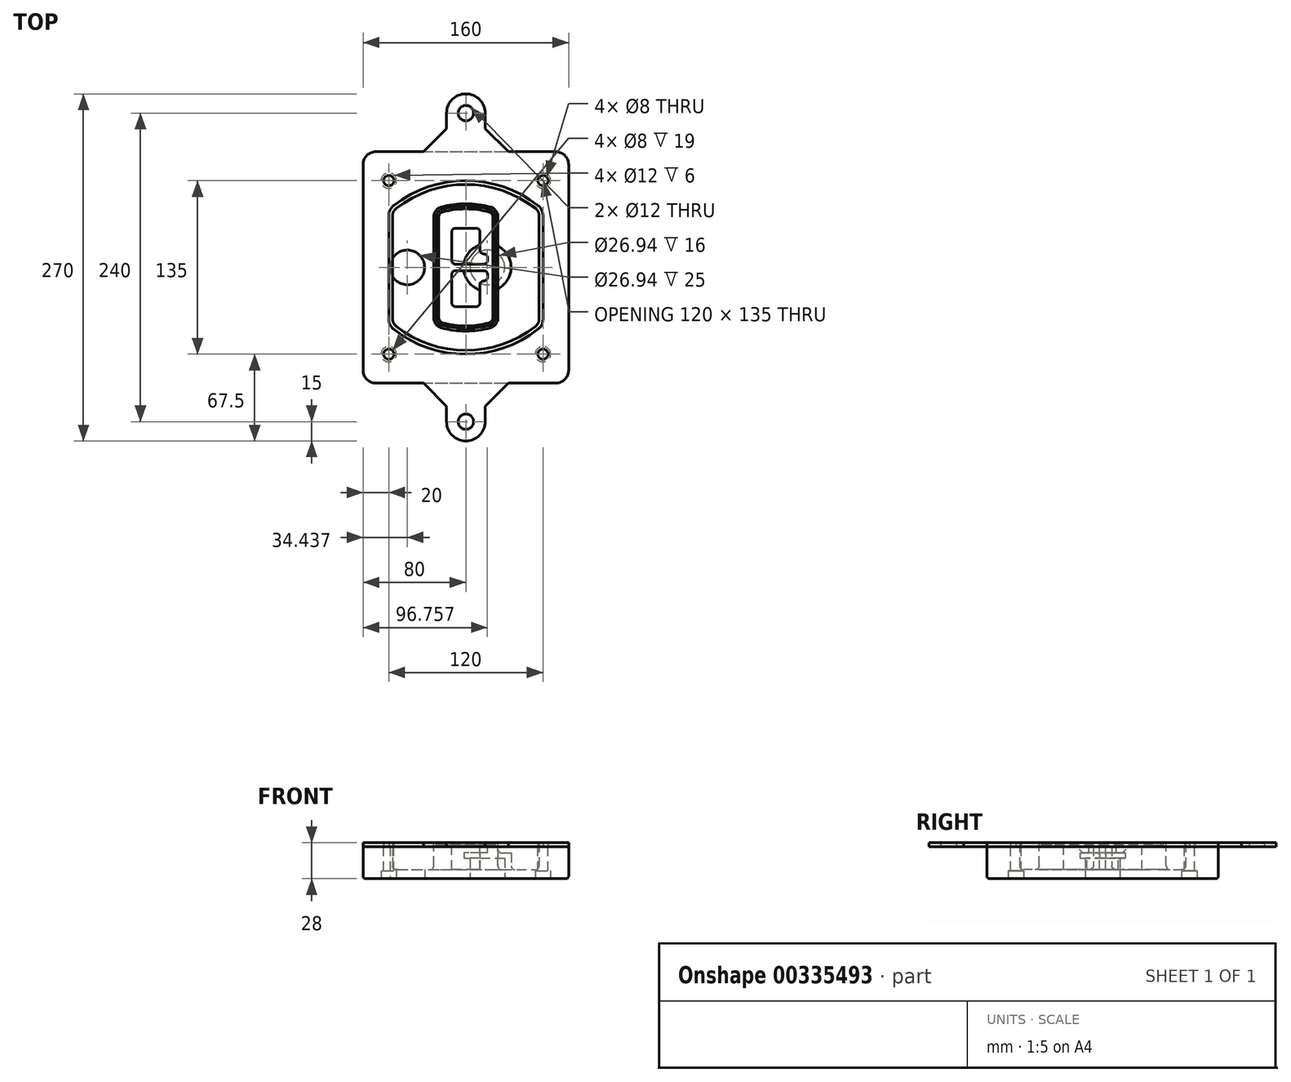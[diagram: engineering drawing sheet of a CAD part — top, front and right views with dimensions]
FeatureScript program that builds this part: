
annotation { "Feature Type Name" : "Feature", "Feature Type Description" : "" }
export const myFeature = defineFeature(function(context is Context, id is Id, definition is map)
    precondition{}
    {
        {
            var Q0;
            Q0=qCreatedBy(makeId("Top.planeOp"),FACE);
            var sketch = newSketch(context, id + "F0", { "sketchPlane" : qUnion([Q0])});
            skPoint(sketch, "E0.rect.middle", {"position": v(0, 0) * mm});
            skLineSegment(sketch, "E1.bottom", {"start": v(-70, -90) * mm, "end": v(70, -90) * mm});
            skLineSegment(sketch, "E1.top", {"start": v(-70, 90) * mm, "end": v(70, 90) * mm});
            skLineSegment(sketch, "E1.left", {"start": v(-80, -80) * mm, "end": v(-80, 80) * mm});
            skLineSegment(sketch, "E1.right", {"start": v(80, -80) * mm, "end": v(80, 80) * mm});
            skLineSegment(sketch, "E2", {"start": v(-80, 90) * mm, "end": v(80, -90) * mm, "construction": true});
            skLineSegment(sketch, "E3", {"start": v(80, 90) * mm, "end": v(-80, -90) * mm, "construction": true});
            skCircle(sketch, "E4", {"center": v(-60, 67.5) * mm, "radius": 4 * mm});
            skCircle(sketch, "E5", {"center": v(60, 67.5) * mm, "radius": 4 * mm});
            skCircle(sketch, "E6", {"center": v(60, -67.5) * mm, "radius": 4 * mm});
            skCircle(sketch, "E7", {"center": v(-60, -67.5) * mm, "radius": 4 * mm});
            skLineSegment(sketch, "E8", {"start": v(-60, 67.5) * mm, "end": v(60, 67.5) * mm, "construction": true});
            skLineSegment(sketch, "E9", {"start": v(60, 67.5) * mm, "end": v(60, -67.5) * mm, "construction": true});
            skLineSegment(sketch, "E10", {"start": v(60, -67.5) * mm, "end": v(-60, -67.5) * mm, "construction": true});
            skLineSegment(sketch, "E11", {"start": v(-60, -67.5) * mm, "end": v(-60, 67.5) * mm, "construction": true});
            skLineSegment(sketch, "E12", {"start": v(-60, 40.3) * mm, "end": v(-60, -40.3) * mm});
            skLineSegment(sketch, "E13", {"start": v(60, 40.3) * mm, "end": v(60, -40.3) * mm});
            skArc(sketch, "E14", {"start": v(56.15, 48.18) * mm, "mid": v(0, 67.5) * mm, "end": v(-56.15, 48.18) * mm});
            skArc(sketch, "E15", {"start": v(-56.15, -48.18) * mm, "mid": v(0, -67.5) * mm, "end": v(56.15, -48.18) * mm});
            skLineSegment(sketch, "E16", {"start": v(-60, 0) * mm, "end": v(60, 0) * mm, "construction": true});
            skPoint(sketch, "E17.visualSharp", {"position": v(-60, -45) * mm});
            skArc(sketch, "E17.filletArc", {"start": v(-60, -40.3) * mm, "mid": v(-58.99, -44.68) * mm, "end": v(-56.15, -48.18) * mm});
            skPoint(sketch, "E18.visualSharp", {"position": v(-60, 45) * mm});
            skArc(sketch, "E18.filletArc", {"start": v(-56.15, 48.18) * mm, "mid": v(-58.99, 44.68) * mm, "end": v(-60, 40.3) * mm});
            skPoint(sketch, "E19.visualSharp", {"position": v(60, 45) * mm});
            skArc(sketch, "E19.filletArc", {"start": v(60, 40.3) * mm, "mid": v(58.99, 44.68) * mm, "end": v(56.15, 48.18) * mm});
            skPoint(sketch, "E20.visualSharp", {"position": v(60, -45) * mm});
            skArc(sketch, "E20.filletArc", {"start": v(56.15, -48.18) * mm, "mid": v(58.99, -44.68) * mm, "end": v(60, -40.3) * mm});
            skPoint(sketch, "E21.visualSharp", {"position": v(-80, 90) * mm});
            skArc(sketch, "E21.filletArc", {"start": v(-70, 90) * mm, "mid": v(-77.07, 87.07) * mm, "end": v(-80, 80) * mm});
            skPoint(sketch, "E22.visualSharp", {"position": v(80, 90) * mm});
            skArc(sketch, "E22.filletArc", {"start": v(80, 80) * mm, "mid": v(77.07, 87.07) * mm, "end": v(70, 90) * mm});
            skPoint(sketch, "E23.visualSharp", {"position": v(80, -90) * mm});
            skArc(sketch, "E23.filletArc", {"start": v(70, -90) * mm, "mid": v(77.07, -87.07) * mm, "end": v(80, -80) * mm});
            skPoint(sketch, "E24.visualSharp", {"position": v(-80, -90) * mm});
            skArc(sketch, "E24.filletArc", {"start": v(-80, -80) * mm, "mid": v(-77.07, -87.07) * mm, "end": v(-70, -90) * mm});
            skArc(sketch, "E25.0", {"start": v(57, 40.3) * mm, "mid": v(56.3, 43.36) * mm, "end": v(54.3, 45.81) * mm});
            skLineSegment(sketch, "E25.1", {"start": v(57, 40.3) * mm, "end": v(57, -40.3) * mm});
            skArc(sketch, "E25.2", {"start": v(54.3, -45.81) * mm, "mid": v(56.3, -43.36) * mm, "end": v(57, -40.3) * mm});
            skArc(sketch, "E25.3", {"start": v(-54.3, -45.81) * mm, "mid": v(0, -64.5) * mm, "end": v(54.3, -45.81) * mm});
            skArc(sketch, "E25.4", {"start": v(-57, -40.3) * mm, "mid": v(-56.3, -43.36) * mm, "end": v(-54.3, -45.81) * mm});
            skArc(sketch, "E25.5", {"start": v(54.3, 45.81) * mm, "mid": v(0, 64.5) * mm, "end": v(-54.3, 45.81) * mm});
            skLineSegment(sketch, "E25.6", {"start": v(-57, 40.3) * mm, "end": v(-57, -40.3) * mm});
            skArc(sketch, "E25.7", {"start": v(-54.3, 45.81) * mm, "mid": v(-56.3, 43.36) * mm, "end": v(-57, 40.3) * mm});
            skArc(sketch, "E26.0", {"start": v(-58.62, 51.33) * mm, "mid": v(-62.58, 46.43) * mm, "end": v(-64, 40.3) * mm});
            skArc(sketch, "E26.1", {"start": v(58.62, 51.33) * mm, "mid": v(0, 71.5) * mm, "end": v(-58.62, 51.33) * mm});
            skArc(sketch, "E26.2", {"start": v(64, 40.3) * mm, "mid": v(62.58, 46.43) * mm, "end": v(58.62, 51.33) * mm});
            skLineSegment(sketch, "E26.3", {"start": v(64, 40.3) * mm, "end": v(64, -40.3) * mm});
            skArc(sketch, "E26.4", {"start": v(58.62, -51.33) * mm, "mid": v(62.58, -46.43) * mm, "end": v(64, -40.3) * mm});
            skLineSegment(sketch, "E26.5", {"start": v(-64, 40.3) * mm, "end": v(-64, -40.3) * mm});
            skArc(sketch, "E26.6", {"start": v(-58.62, -51.33) * mm, "mid": v(0, -71.5) * mm, "end": v(58.62, -51.33) * mm});
            skArc(sketch, "E26.7", {"start": v(-64, -40.3) * mm, "mid": v(-62.58, -46.43) * mm, "end": v(-58.62, -51.33) * mm});
            skSolve(sketch);
        }
        {
            var Q0;
            Q0=makeQuery(id+"F0.imprint","IMPRINT",FACE,{"disambiguationData":[TD([[makeQuery(id+"F0.imprint","IMPRINT",EDGE,{"derivedFrom":sQuery(id+"F0.wireOp",EDGE,"E1.bottom")}),1.0]])]});
            var Q1;
            Q1=makeQuery(id+"F0.imprint","IMPRINT",FACE,{"disambiguationData":[TD([[makeQuery(id+"F0.imprint","IMPRINT",EDGE,{"derivedFrom":sQuery(id+"F0.wireOp",EDGE,"E12")}),1.0]])]});
            var Q2;
            Q2=makeQuery(id+"F0.imprint","IMPRINT",FACE,{"disambiguationData":[TD([[makeQuery(id+"F0.imprint","IMPRINT",EDGE,{"derivedFrom":sQuery(id+"F0.wireOp",EDGE,"E25.0")}),1.0]])]});
            var Q3;
            Q3=makeQuery(id+"F0.imprint","IMPRINT",FACE,{"disambiguationData":[TD([[makeQuery(id+"F0.imprint","IMPRINT",EDGE,{"derivedFrom":sQuery(id+"F0.wireOp",EDGE,"E12")}),-1.0]])]});
            extrude(context, id + "F1", {"entities" : qUnion([Q0, Q1, Q2, Q3]), "oppositeDirection" : true, "depth" : 25 * mm});
        }
        {
            var Q0;
            Q0=makeQuery(id+"F0.imprint","IMPRINT",FACE,{"disambiguationData":[TD([[makeQuery(id+"F0.imprint","IMPRINT",EDGE,{"derivedFrom":sQuery(id+"F0.wireOp",EDGE,"E12")}),1.0]])]});
            extrude(context, id + "F2", {"entities" : qUnion([Q0]), "operationType" : NewBodyOperationType.ADD, "depth" : 3 * mm});
        }
        {
            var Q0;
            Q0=makeQuery(id+"F0.imprint","IMPRINT",FACE,{"disambiguationData":[TD([[makeQuery(id+"F0.imprint","IMPRINT",EDGE,{"derivedFrom":sQuery(id+"F0.wireOp",EDGE,"E25.0")}),1.0]])]});
            extrude(context, id + "F3", {"entities" : qUnion([Q0]), "operationType" : NewBodyOperationType.REMOVE, "oppositeDirection" : true, "depth" : 18 * mm});
        }
        {
            var Q0;
            Q0=makeQuery(id+"F2.opExtrude","CAP_FACE",FACE,{"disambiguationData":[OSD([sQuery(id+"F0.wireOp",EDGE,"E12"),sQuery(id+"F0.wireOp",EDGE,"E13"),sQuery(id+"F0.wireOp",EDGE,"E14"),sQuery(id+"F0.wireOp",EDGE,"E15"),sQuery(id+"F0.wireOp",EDGE,"E17.filletArc"),sQuery(id+"F0.wireOp",EDGE,"E18.filletArc"),sQuery(id+"F0.wireOp",EDGE,"E19.filletArc"),sQuery(id+"F0.wireOp",EDGE,"E20.filletArc"),sQuery(id+"F0.wireOp",EDGE,"E25.0"),sQuery(id+"F0.wireOp",EDGE,"E25.1"),sQuery(id+"F0.wireOp",EDGE,"E25.2"),sQuery(id+"F0.wireOp",EDGE,"E25.3"),sQuery(id+"F0.wireOp",EDGE,"E25.4"),sQuery(id+"F0.wireOp",EDGE,"E25.5"),sQuery(id+"F0.wireOp",EDGE,"E25.6"),sQuery(id+"F0.wireOp",EDGE,"E25.7")])],"isStart":false});
            var sketch = newSketch(context, id + "F4", { "sketchPlane" : qUnion([Q0])});
            skArc(sketch, "E27.0", {"start": v(-19.08, -46.97) * mm, "mid": v(0, -49.5) * mm, "end": v(19.08, -46.97) * mm});
            skArc(sketch, "E28.0", {"start": v(19.08, 46.97) * mm, "mid": v(0, 49.5) * mm, "end": v(-19.08, 46.97) * mm});
            skLineSegment(sketch, "E29", {"start": v(-25, 39.25) * mm, "end": v(-25, -39.25) * mm});
            skLineSegment(sketch, "E30", {"start": v(25, 39.25) * mm, "end": v(25, -39.25) * mm});
            skLineSegment(sketch, "E31", {"start": v(-25, 45.1) * mm, "end": v(25, 45.1) * mm, "construction": true});
            skLineSegment(sketch, "E32", {"start": v(-25, -45.1) * mm, "end": v(25, -45.1) * mm, "construction": true});
            skPoint(sketch, "E33.visualSharp", {"position": v(-25, 45.1) * mm});
            skArc(sketch, "E33.filletArc", {"start": v(-19.08, 46.97) * mm, "mid": v(-23.35, 44.11) * mm, "end": v(-25, 39.25) * mm});
            skPoint(sketch, "E34.visualSharp", {"position": v(25, 45.1) * mm});
            skArc(sketch, "E34.filletArc", {"start": v(25, 39.25) * mm, "mid": v(23.35, 44.11) * mm, "end": v(19.08, 46.97) * mm});
            skPoint(sketch, "E35.visualSharp", {"position": v(25, -45.1) * mm});
            skArc(sketch, "E35.filletArc", {"start": v(19.08, -46.97) * mm, "mid": v(23.35, -44.11) * mm, "end": v(25, -39.25) * mm});
            skPoint(sketch, "E36.visualSharp", {"position": v(-25, -45.1) * mm});
            skArc(sketch, "E36.filletArc", {"start": v(-25, -39.25) * mm, "mid": v(-23.35, -44.11) * mm, "end": v(-19.08, -46.97) * mm});
            skArc(sketch, "E37.0", {"start": v(54.3, 45.81) * mm, "mid": v(0, 64.5) * mm, "end": v(-54.3, 45.81) * mm});
            skArc(sketch, "E37.1", {"start": v(-54.3, 45.81) * mm, "mid": v(-56.3, 43.36) * mm, "end": v(-57, 40.3) * mm});
            skLineSegment(sketch, "E37.2", {"start": v(-57, 40.3) * mm, "end": v(-57, -40.3) * mm});
            skArc(sketch, "E37.3", {"start": v(-57, -40.3) * mm, "mid": v(-56.3, -43.36) * mm, "end": v(-54.3, -45.81) * mm});
            skArc(sketch, "E37.4", {"start": v(-54.3, -45.81) * mm, "mid": v(0, -64.5) * mm, "end": v(54.3, -45.81) * mm});
            skArc(sketch, "E37.5", {"start": v(54.3, -45.81) * mm, "mid": v(56.3, -43.36) * mm, "end": v(57, -40.3) * mm});
            skLineSegment(sketch, "E37.6", {"start": v(57, 40.3) * mm, "end": v(57, -40.3) * mm});
            skArc(sketch, "E37.7", {"start": v(57, 40.3) * mm, "mid": v(56.3, 43.36) * mm, "end": v(54.3, 45.81) * mm});
            skLineSegment(sketch, "E38.0", {"start": v(23, 39.25) * mm, "end": v(23, -39.25) * mm});
            skArc(sketch, "E38.1", {"start": v(18.56, -45.04) * mm, "mid": v(21.76, -42.9) * mm, "end": v(23, -39.25) * mm});
            skArc(sketch, "E38.2", {"start": v(-18.56, -45.04) * mm, "mid": v(0, -47.5) * mm, "end": v(18.56, -45.04) * mm});
            skArc(sketch, "E38.3", {"start": v(-23, -39.25) * mm, "mid": v(-21.76, -42.9) * mm, "end": v(-18.56, -45.04) * mm});
            skLineSegment(sketch, "E38.4", {"start": v(-23, 39.25) * mm, "end": v(-23, -39.25) * mm});
            skArc(sketch, "E38.5", {"start": v(23, 39.25) * mm, "mid": v(21.76, 42.9) * mm, "end": v(18.56, 45.04) * mm});
            skArc(sketch, "E38.6", {"start": v(-18.56, 45.04) * mm, "mid": v(-21.76, 42.9) * mm, "end": v(-23, 39.25) * mm});
            skArc(sketch, "E38.7", {"start": v(18.56, 45.04) * mm, "mid": v(0, 47.5) * mm, "end": v(-18.56, 45.04) * mm});
            skArc(sketch, "E39.0", {"start": v(21, 39.25) * mm, "mid": v(20.18, 41.68) * mm, "end": v(18.04, 43.1) * mm});
            skLineSegment(sketch, "E39.1", {"start": v(21, 39.25) * mm, "end": v(21, -39.25) * mm});
            skArc(sketch, "E39.2", {"start": v(18.04, -43.1) * mm, "mid": v(20.18, -41.68) * mm, "end": v(21, -39.25) * mm});
            skArc(sketch, "E39.3", {"start": v(-18.04, -43.1) * mm, "mid": v(0, -45.5) * mm, "end": v(18.04, -43.1) * mm});
            skArc(sketch, "E39.4", {"start": v(-21, -39.25) * mm, "mid": v(-20.18, -41.68) * mm, "end": v(-18.04, -43.1) * mm});
            skArc(sketch, "E39.5", {"start": v(18.04, 43.1) * mm, "mid": v(0, 45.5) * mm, "end": v(-18.04, 43.1) * mm});
            skLineSegment(sketch, "E39.6", {"start": v(-21, 39.25) * mm, "end": v(-21, -39.25) * mm});
            skArc(sketch, "E39.7", {"start": v(-18.04, 43.1) * mm, "mid": v(-20.18, 41.68) * mm, "end": v(-21, 39.25) * mm});
            skLineSegment(sketch, "E40", {"start": v(-25, 0) * mm, "end": v(25, 0) * mm, "construction": true});
            skLineSegment(sketch, "E41", {"start": v(-11, 5.5) * mm, "end": v(-11, 27.5) * mm});
            skLineSegment(sketch, "E42", {"start": v(-8, 30.5) * mm, "end": v(8, 30.5) * mm});
            skLineSegment(sketch, "E43", {"start": v(11, 27.5) * mm, "end": v(11, 13.5) * mm});
            skLineSegment(sketch, "E44", {"start": v(14, 10.5) * mm, "end": v(14, 10.5) * mm});
            skLineSegment(sketch, "E45", {"start": v(17, 7.5) * mm, "end": v(17, 5.5) * mm});
            skLineSegment(sketch, "E46", {"start": v(14, 2.5) * mm, "end": v(-8, 2.5) * mm});
            skPoint(sketch, "E47.visualSharp", {"position": v(-11, 30.5) * mm});
            skArc(sketch, "E47.filletArc", {"start": v(-8, 30.5) * mm, "mid": v(-10.12, 29.62) * mm, "end": v(-11, 27.5) * mm});
            skPoint(sketch, "E48.visualSharp", {"position": v(11, 30.5) * mm});
            skArc(sketch, "E48.filletArc", {"start": v(11, 27.5) * mm, "mid": v(10.12, 29.62) * mm, "end": v(8, 30.5) * mm});
            skPoint(sketch, "E49.visualSharp", {"position": v(11, 10.5) * mm});
            skArc(sketch, "E49.filletArc", {"start": v(11, 13.5) * mm, "mid": v(11.88, 11.38) * mm, "end": v(14, 10.5) * mm});
            skPoint(sketch, "E50.visualSharp", {"position": v(17, 10.5) * mm});
            skArc(sketch, "E50.filletArc", {"start": v(17, 7.5) * mm, "mid": v(16.12, 9.62) * mm, "end": v(14, 10.5) * mm});
            skPoint(sketch, "E51.visualSharp", {"position": v(17, 2.5) * mm});
            skArc(sketch, "E51.filletArc", {"start": v(14, 2.5) * mm, "mid": v(16.12, 3.38) * mm, "end": v(17, 5.5) * mm});
            skPoint(sketch, "E52.visualSharp", {"position": v(-11, 2.5) * mm});
            skArc(sketch, "E52.filletArc", {"start": v(-11, 5.5) * mm, "mid": v(-10.12, 3.38) * mm, "end": v(-8, 2.5) * mm});
            skLineSegment(sketch, "E53.0.MirrorCS", {"start": v(14, -2.5) * mm, "end": v(-8, -2.5) * mm});
            skArc(sketch, "E54.0.MirrorCS", {"start": v(-11, -5.5) * mm, "mid": v(-10.12, -3.38) * mm, "end": v(-8, -2.5) * mm});
            skLineSegment(sketch, "E55.0.MirrorCS", {"start": v(-11, -5.5) * mm, "end": v(-11, -27.5) * mm});
            skArc(sketch, "E56.0.MirrorCS", {"start": v(-8, -30.5) * mm, "mid": v(-10.12, -29.62) * mm, "end": v(-11, -27.5) * mm});
            skLineSegment(sketch, "E57.0.MirrorCS", {"start": v(-8, -30.5) * mm, "end": v(8, -30.5) * mm});
            skArc(sketch, "E58.0.MirrorCS", {"start": v(11, -27.5) * mm, "mid": v(10.12, -29.62) * mm, "end": v(8, -30.5) * mm});
            skLineSegment(sketch, "E59.0.MirrorCS", {"start": v(11, -27.5) * mm, "end": v(11, -13.5) * mm});
            skArc(sketch, "E60.0.MirrorCS", {"start": v(11, -13.5) * mm, "mid": v(11.88, -11.38) * mm, "end": v(14, -10.5) * mm});
            skArc(sketch, "E61.0.MirrorCS", {"start": v(17, -7.5) * mm, "mid": v(16.12, -9.62) * mm, "end": v(14, -10.5) * mm});
            skLineSegment(sketch, "E62.0.MirrorCS", {"start": v(17, -7.5) * mm, "end": v(17, -5.5) * mm});
            skArc(sketch, "E63.0.MirrorCS", {"start": v(14, -2.5) * mm, "mid": v(16.12, -3.38) * mm, "end": v(17, -5.5) * mm});
            skSolve(sketch);
        }
        {
            var Q0;
            Q0=makeQuery(id+"F4.imprint","IMPRINT",FACE,{"disambiguationData":[TD([[makeQuery(id+"F4.imprint","IMPRINT",EDGE,{"derivedFrom":sQuery(id+"F4.wireOp",EDGE,"E27.0")}),1.0]])]});
            var Q1;
            Q1=makeQuery(id+"F4.imprint","IMPRINT",FACE,{"disambiguationData":[TD([[makeQuery(id+"F4.imprint","IMPRINT",EDGE,{"derivedFrom":sQuery(id+"F4.wireOp",EDGE,"E38.0")}),-1.0]])]});
            var Q2;
            Q2=makeQuery(id+"F4.imprint","IMPRINT",FACE,{"disambiguationData":[TD([[makeQuery(id+"F4.imprint","IMPRINT",EDGE,{"derivedFrom":sQuery(id+"F4.wireOp",EDGE,"E39.0")}),1.0]])]});
            extrude(context, id + "F5", {"entities" : qUnion([Q0, Q1, Q2]), "operationType" : NewBodyOperationType.ADD, "endBound" : BoundingType.UP_TO_NEXT, "oppositeDirection" : true, "depth" : 25 * mm});
        }
        {
            var Q0;
            Q0=makeQuery(id+"F4.imprint","IMPRINT",FACE,{"disambiguationData":[TD([[makeQuery(id+"F4.imprint","IMPRINT",EDGE,{"derivedFrom":sQuery(id+"F4.wireOp",EDGE,"E38.0")}),-1.0]])]});
            extrude(context, id + "F6", {"entities" : qUnion([Q0]), "operationType" : NewBodyOperationType.REMOVE, "oppositeDirection" : true, "depth" : 2 * mm});
        }
        {
            var Q0;
            Q0=makeQuery(id+"F1.opExtrude","CAP_FACE",FACE,{"disambiguationData":[OSD([sQuery(id+"F0.wireOp",EDGE,"E1.bottom"),sQuery(id+"F0.wireOp",EDGE,"E1.top"),sQuery(id+"F0.wireOp",EDGE,"E1.left"),sQuery(id+"F0.wireOp",EDGE,"E1.right"),sQuery(id+"F0.wireOp",EDGE,"E4"),sQuery(id+"F0.wireOp",EDGE,"E5"),sQuery(id+"F0.wireOp",EDGE,"E6"),sQuery(id+"F0.wireOp",EDGE,"E7"),sQuery(id+"F0.wireOp",EDGE,"E21.filletArc"),sQuery(id+"F0.wireOp",EDGE,"E22.filletArc"),sQuery(id+"F0.wireOp",EDGE,"E23.filletArc"),sQuery(id+"F0.wireOp",EDGE,"E24.filletArc")])],"isStart":false});
            var sketch = newSketch(context, id + "F7", { "sketchPlane" : qUnion([Q0])});
            skCircle(sketch, "E64", {"center": v(16.76, 0) * mm, "radius": 13.47 * mm});
            skCircle(sketch, "E65", {"center": v(-45.56, 0) * mm, "radius": 13.47 * mm});
            skLineSegment(sketch, "E66", {"start": v(80, 0) * mm, "end": v(-80, 0) * mm});
            skCircle(sketch, "E67", {"center": v(16.76, 0) * mm, "radius": 18.47 * mm});
            skCircle(sketch, "E68", {"center": v(60, -67.5) * mm, "radius": 6 * mm});
            skCircle(sketch, "E69", {"center": v(-60, -67.5) * mm, "radius": 6 * mm});
            skCircle(sketch, "E70", {"center": v(-60, 67.5) * mm, "radius": 6 * mm});
            skCircle(sketch, "E71", {"center": v(60, 67.5) * mm, "radius": 6 * mm});
            skSolve(sketch);
        }
        {
            var Q0;
            {var subQ1=sQuery(id+"F7.wireOp",EDGE,"E66");var subQ4=sQuery(id+"F7.wireOp",EDGE,"E64");var subQ6=makeQuery(id+"F7.imprint","INTERSECT",VERTEX,{"disambiguationData":[OD(0.0)],"derivedFrom":[subQ4,subQ1]});Q0=makeQuery(id+"F7.imprint","IMPRINT",FACE,{"disambiguationData":[TD([[makeQuery(id+"F7.imprint","IMPRINT",EDGE,{"disambiguationData":[TD([[subQ6,-1.0]])],"derivedFrom":subQ4}),-1.0]])]});}
            var Q1;
            {var subQ0=sQuery(id+"F7.wireOp",EDGE,"E66");var subQ1=sQuery(id+"F7.wireOp",EDGE,"E64");var subQ3=makeQuery(id+"F7.imprint","INTERSECT",VERTEX,{"disambiguationData":[OD(0.0)],"derivedFrom":[subQ1,subQ0]});Q1=makeQuery(id+"F7.imprint","IMPRINT",FACE,{"disambiguationData":[TD([[makeQuery(id+"F7.imprint","IMPRINT",EDGE,{"disambiguationData":[TD([[subQ3,-1.0]])],"derivedFrom":subQ1}),1.0]])]});}
            var Q2;
            {var subQ0=sQuery(id+"F7.wireOp",EDGE,"E66");var subQ1=sQuery(id+"F7.wireOp",EDGE,"E64");var subQ3=makeQuery(id+"F7.imprint","INTERSECT",VERTEX,{"disambiguationData":[OD(0.0)],"derivedFrom":[subQ1,subQ0]});Q2=makeQuery(id+"F7.imprint","IMPRINT",FACE,{"disambiguationData":[TD([[makeQuery(id+"F7.imprint","IMPRINT",EDGE,{"disambiguationData":[TD([[subQ3,1.0]])],"derivedFrom":subQ1}),1.0]])]});}
            var Q3;
            {var subQ1=sQuery(id+"F7.wireOp",EDGE,"E66");var subQ4=sQuery(id+"F7.wireOp",EDGE,"E64");var subQ6=makeQuery(id+"F7.imprint","INTERSECT",VERTEX,{"disambiguationData":[OD(0.0)],"derivedFrom":[subQ4,subQ1]});Q3=makeQuery(id+"F7.imprint","IMPRINT",FACE,{"disambiguationData":[TD([[makeQuery(id+"F7.imprint","IMPRINT",EDGE,{"disambiguationData":[TD([[subQ6,1.0]])],"derivedFrom":subQ4}),-1.0]])]});}
            extrude(context, id + "F8", {"entities" : qUnion([Q0, Q1, Q2, Q3]), "operationType" : NewBodyOperationType.ADD, "oppositeDirection" : true, "depth" : 20 * mm});
        }
        {
            var Q0;
            {var subQ0=sQuery(id+"F7.wireOp",EDGE,"E66");var subQ1=sQuery(id+"F7.wireOp",EDGE,"E64");var subQ3=makeQuery(id+"F7.imprint","INTERSECT",VERTEX,{"disambiguationData":[OD(0.0)],"derivedFrom":[subQ1,subQ0]});Q0=makeQuery(id+"F7.imprint","IMPRINT",FACE,{"disambiguationData":[TD([[makeQuery(id+"F7.imprint","IMPRINT",EDGE,{"disambiguationData":[TD([[subQ3,-1.0]])],"derivedFrom":subQ1}),1.0]])]});}
            var Q1;
            {var subQ0=sQuery(id+"F7.wireOp",EDGE,"E66");var subQ1=sQuery(id+"F7.wireOp",EDGE,"E64");var subQ3=makeQuery(id+"F7.imprint","INTERSECT",VERTEX,{"disambiguationData":[OD(0.0)],"derivedFrom":[subQ1,subQ0]});Q1=makeQuery(id+"F7.imprint","IMPRINT",FACE,{"disambiguationData":[TD([[makeQuery(id+"F7.imprint","IMPRINT",EDGE,{"disambiguationData":[TD([[subQ3,1.0]])],"derivedFrom":subQ1}),1.0]])]});}
            extrude(context, id + "F9", {"entities" : qUnion([Q0, Q1]), "operationType" : NewBodyOperationType.REMOVE, "oppositeDirection" : true, "depth" : 16 * mm});
        }
        {
            var Q0;
            {var subQ0=sQuery(id+"F7.wireOp",EDGE,"E66");var subQ1=sQuery(id+"F7.wireOp",EDGE,"E65");var subQ3=makeQuery(id+"F7.imprint","INTERSECT",VERTEX,{"disambiguationData":[OD(0.0)],"derivedFrom":[subQ1,subQ0]});Q0=makeQuery(id+"F7.imprint","IMPRINT",FACE,{"disambiguationData":[TD([[makeQuery(id+"F7.imprint","IMPRINT",EDGE,{"disambiguationData":[TD([[subQ3,-1.0]])],"derivedFrom":subQ1}),1.0]])]});}
            var Q1;
            {var subQ0=sQuery(id+"F7.wireOp",EDGE,"E66");var subQ1=sQuery(id+"F7.wireOp",EDGE,"E65");var subQ3=makeQuery(id+"F7.imprint","INTERSECT",VERTEX,{"disambiguationData":[OD(0.0)],"derivedFrom":[subQ1,subQ0]});Q1=makeQuery(id+"F7.imprint","IMPRINT",FACE,{"disambiguationData":[TD([[makeQuery(id+"F7.imprint","IMPRINT",EDGE,{"disambiguationData":[TD([[subQ3,1.0]])],"derivedFrom":subQ1}),1.0]])]});}
            extrude(context, id + "F10", {"entities" : qUnion([Q0, Q1]), "operationType" : NewBodyOperationType.REMOVE, "oppositeDirection" : true, "depth" : 25 * mm});
        }
        {
            var Q0;
            Q0=makeQuery(id+"F7.imprint","IMPRINT",FACE,{"disambiguationData":[TD([[makeQuery(id+"F7.imprint","IMPRINT",EDGE,{"derivedFrom":sQuery(id+"F7.wireOp",EDGE,"E68")}),1.0]])]});
            var Q1;
            Q1=makeQuery(id+"F7.imprint","IMPRINT",FACE,{"disambiguationData":[TD([[makeQuery(id+"F7.imprint","IMPRINT",EDGE,{"derivedFrom":makeQuery(id+"F1.opExtrude","CAP_EDGE",EDGE,{"disambiguationData":[OSD([sQuery(id+"F0.wireOp",EDGE,"E5")])],"isStart":false})}),-1.0]])]});
            var Q2;
            Q2=makeQuery(id+"F7.imprint","IMPRINT",FACE,{"disambiguationData":[TD([[makeQuery(id+"F7.imprint","IMPRINT",EDGE,{"derivedFrom":sQuery(id+"F7.wireOp",EDGE,"E69")}),1.0]])]});
            var Q3;
            Q3=makeQuery(id+"F7.imprint","IMPRINT",FACE,{"disambiguationData":[TD([[makeQuery(id+"F7.imprint","IMPRINT",EDGE,{"derivedFrom":makeQuery(id+"F1.opExtrude","CAP_EDGE",EDGE,{"disambiguationData":[OSD([sQuery(id+"F0.wireOp",EDGE,"E4")])],"isStart":false})}),-1.0]])]});
            var Q4;
            Q4=makeQuery(id+"F7.imprint","IMPRINT",FACE,{"disambiguationData":[TD([[makeQuery(id+"F7.imprint","IMPRINT",EDGE,{"derivedFrom":sQuery(id+"F7.wireOp",EDGE,"E70")}),1.0]])]});
            var Q5;
            Q5=makeQuery(id+"F7.imprint","IMPRINT",FACE,{"disambiguationData":[TD([[makeQuery(id+"F7.imprint","IMPRINT",EDGE,{"derivedFrom":makeQuery(id+"F1.opExtrude","CAP_EDGE",EDGE,{"disambiguationData":[OSD([sQuery(id+"F0.wireOp",EDGE,"E7")])],"isStart":false})}),-1.0]])]});
            var Q6;
            Q6=makeQuery(id+"F7.imprint","IMPRINT",FACE,{"disambiguationData":[TD([[makeQuery(id+"F7.imprint","IMPRINT",EDGE,{"derivedFrom":sQuery(id+"F7.wireOp",EDGE,"E71")}),1.0]])]});
            var Q7;
            Q7=makeQuery(id+"F7.imprint","IMPRINT",FACE,{"disambiguationData":[TD([[makeQuery(id+"F7.imprint","IMPRINT",EDGE,{"derivedFrom":makeQuery(id+"F1.opExtrude","CAP_EDGE",EDGE,{"disambiguationData":[OSD([sQuery(id+"F0.wireOp",EDGE,"E6")])],"isStart":false})}),-1.0]])]});
            extrude(context, id + "F11", {"entities" : qUnion([Q0, Q1, Q2, Q3, Q4, Q5, Q6, Q7]), "operationType" : NewBodyOperationType.REMOVE, "oppositeDirection" : true, "depth" : 6 * mm});
        }
        {
            var Q0;
            Q0=makeQuery(id+"F9.boolean.opBoolean","COPY",FACE,{"derivedFrom":makeQuery(id+"F9.opExtrude","CAP_FACE",FACE,{"disambiguationData":[OSD([sQuery(id+"F7.wireOp",EDGE,"E64")])],"isStart":false})});
            var sketch = newSketch(context, id + "F12", { "sketchPlane" : qUnion([Q0])});
            skArc(sketch, "E72.0", {"start": v(11, 17.55) * mm, "mid": v(2.57, 11.82) * mm, "end": v(-1.54, 2.5) * mm});
            skArc(sketch, "E72.1", {"start": v(-1.54, -2.5) * mm, "mid": v(2.57, -11.82) * mm, "end": v(11, -17.55) * mm});
            skLineSegment(sketch, "E73", {"start": v(-1.54, -2.5) * mm, "end": v(14, -2.5) * mm});
            skLineSegment(sketch, "E74.0", {"start": v(14, 2.5) * mm, "end": v(-1.54, 2.5) * mm});
            skArc(sketch, "E74.1", {"start": v(14, 2.5) * mm, "mid": v(16.12, 3.38) * mm, "end": v(17, 5.5) * mm});
            skLineSegment(sketch, "E74.2", {"start": v(17, 7.5) * mm, "end": v(17, 5.5) * mm});
            skArc(sketch, "E74.3", {"start": v(17, 7.5) * mm, "mid": v(16.12, 9.62) * mm, "end": v(14, 10.5) * mm});
            skArc(sketch, "E74.4", {"start": v(11, 13.5) * mm, "mid": v(11.88, 11.38) * mm, "end": v(14, 10.5) * mm});
            skLineSegment(sketch, "E74.5", {"start": v(11, 17.55) * mm, "end": v(11, 13.5) * mm});
            skLineSegment(sketch, "E74.7", {"start": v(14, -2.5) * mm, "end": v(-1.54, -2.5) * mm});
            skArc(sketch, "E74.8", {"start": v(14, -2.5) * mm, "mid": v(16.12, -3.38) * mm, "end": v(17, -5.5) * mm});
            skLineSegment(sketch, "E74.9", {"start": v(17, -7.5) * mm, "end": v(17, -5.5) * mm});
            skArc(sketch, "E74.10", {"start": v(17, -7.5) * mm, "mid": v(16.12, -9.62) * mm, "end": v(14, -10.5) * mm});
            skArc(sketch, "E74.11", {"start": v(11, -13.5) * mm, "mid": v(11.88, -11.38) * mm, "end": v(14, -10.5) * mm});
            skLineSegment(sketch, "E74.12", {"start": v(11, -17.55) * mm, "end": v(11, -13.5) * mm});
            skPoint(sketch, "E75.orphan", {"position": v(11, -27.5) * mm});
            skPoint(sketch, "E76.orphan", {"position": v(-8, -2.5) * mm});
            skPoint(sketch, "E77.orphan", {"position": v(-8, 2.5) * mm});
            skPoint(sketch, "E78.orphan", {"position": v(11, 27.5) * mm});
            skSolve(sketch);
        }
        {
            var Q0;
            {var subQ7=sQuery(id+"F12.wireOp",EDGE,"E72.0");var subQ14=sQuery(id+"F12.wireOp",EDGE,"E72.1");var subQ16=sQuery(id+"F12.wireOp",EDGE,"E74.1");var subQ18=sQuery(id+"F12.wireOp",EDGE,"E74.8");Q0=qUnion([makeQuery(id+"F12.imprint","IMPRINT",FACE,{"disambiguationData":[TD([[makeQuery(id+"F12.imprint","IMPRINT",EDGE,{"derivedFrom":subQ7}),1.0]])]}),makeQuery(id+"F12.imprint","IMPRINT",FACE,{"disambiguationData":[TD([[makeQuery(id+"F12.imprint","IMPRINT",EDGE,{"derivedFrom":subQ14}),1.0]])]}),makeQuery(id+"F12.imprint","IMPRINT",FACE,{"disambiguationData":[TD([[makeQuery(id+"F12.imprint","IMPRINT",EDGE,{"derivedFrom":subQ16}),1.0]])]}),makeQuery(id+"F12.imprint","IMPRINT",FACE,{"disambiguationData":[TD([[makeQuery(id+"F12.imprint","IMPRINT",EDGE,{"derivedFrom":subQ18}),-1.0]])]})]);}
            var Q1;
            Q1=makeQuery(id+"F5.boolean.opBoolean","SPLIT",FACE,{"disambiguationData":[TD([makeQuery(id+"F5.opExtrude","SWEPT_FACE",FACE,{"disambiguationData":[OSD([sQuery(id+"F4.wireOp",EDGE,"E41")])]})])],"derivedFrom":makeQuery(id+"F3.boolean.opBoolean","COPY",FACE,{"derivedFrom":makeQuery(id+"F3.opExtrude","CAP_FACE",FACE,{"disambiguationData":[OSD([sQuery(id+"F0.wireOp",EDGE,"E25.0"),sQuery(id+"F0.wireOp",EDGE,"E25.1"),sQuery(id+"F0.wireOp",EDGE,"E25.2"),sQuery(id+"F0.wireOp",EDGE,"E25.3"),sQuery(id+"F0.wireOp",EDGE,"E25.4"),sQuery(id+"F0.wireOp",EDGE,"E25.5"),sQuery(id+"F0.wireOp",EDGE,"E25.6"),sQuery(id+"F0.wireOp",EDGE,"E25.7")])],"isStart":false})})});
            extrude(context, id + "F13", {"entities" : qUnion([Q0]), "operationType" : NewBodyOperationType.REMOVE, "endBound" : BoundingType.UP_TO_SURFACE, "endBoundEntityFace" : qUnion([Q1]), "depth" : 25 * mm});
        }
        {
            var Q0;
            Q0=makeQuery(id+"F3.boolean.opBoolean","COPY",EDGE,{"derivedFrom":makeQuery(id+"F3.opExtrude","CAP_EDGE",EDGE,{"disambiguationData":[OSD([sQuery(id+"F0.wireOp",EDGE,"E25.6")])],"isStart":false})});
            var Q1;
            Q1=makeQuery(id+"F8.boolean.opBoolean","INTERSECT",EDGE,{"derivedFrom":[makeQuery(id+"F5.opExtrude","SWEPT_FACE",FACE,{"disambiguationData":[OSD([sQuery(id+"F4.wireOp",EDGE,"E30")])]}),makeQuery(id+"F8.opExtrude","CAP_FACE",FACE,{"disambiguationData":[OSD([sQuery(id+"F7.wireOp",EDGE,"E67")])],"isStart":false})]});
            var Q2;
            Q2=makeQuery(id+"F8.boolean.opBoolean","INTERSECT",EDGE,{"disambiguationData":[OD(1.0)],"derivedFrom":[makeQuery(id+"F5.opExtrude","SWEPT_FACE",FACE,{"disambiguationData":[OSD([sQuery(id+"F4.wireOp",EDGE,"E30")])]}),makeQuery(id+"F8.opExtrude","SWEPT_FACE",FACE,{"disambiguationData":[OSD([sQuery(id+"F7.wireOp",EDGE,"E67")])]})]});
            var Q3;
            {var subQ0=sQuery(id+"F4.wireOp",EDGE,"E30");Q3=makeQuery(id+"F8.boolean.opBoolean","SPLIT",EDGE,{"disambiguationData":[TD([makeQuery(id+"F5.opExtrude","SWEPT_FACE",FACE,{"disambiguationData":[OSD([sQuery(id+"F4.wireOp",EDGE,"E35.filletArc")])]})])],"derivedFrom":makeQuery(id+"F5.opExtrude","CAP_EDGE",EDGE,{"disambiguationData":[OSD([subQ0])],"isStart":false})});}
            var Q4;
            {var subQ0=sQuery(id+"F0.wireOp",EDGE,"E25.7");var subQ1=sQuery(id+"F0.wireOp",EDGE,"E25.1");var subQ2=sQuery(id+"F0.wireOp",EDGE,"E25.6");var subQ3=sQuery(id+"F0.wireOp",EDGE,"E25.5");var subQ4=sQuery(id+"F0.wireOp",EDGE,"E25.4");var subQ5=sQuery(id+"F0.wireOp",EDGE,"E25.0");var subQ6=sQuery(id+"F0.wireOp",EDGE,"E25.2");var subQ7=sQuery(id+"F0.wireOp",EDGE,"E25.3");Q4=makeQuery(id+"F8.boolean.opBoolean","INTERSECT",EDGE,{"derivedFrom":[makeQuery(id+"F5.boolean.opBoolean","SPLIT",FACE,{"disambiguationData":[TD([makeQuery(id+"F2.opExtrude","SWEPT_FACE",FACE,{"disambiguationData":[OSD([subQ5])]})])],"derivedFrom":makeQuery(id+"F3.boolean.opBoolean","COPY",FACE,{"derivedFrom":makeQuery(id+"F3.opExtrude","CAP_FACE",FACE,{"disambiguationData":[OSD([subQ5,subQ1,subQ6,subQ7,subQ4,subQ3,subQ2,subQ0])],"isStart":false})})}),makeQuery(id+"F8.opExtrude","SWEPT_FACE",FACE,{"disambiguationData":[OSD([sQuery(id+"F7.wireOp",EDGE,"E67")])]})]});}
            var Q5;
            Q5=makeQuery(id+"F8.boolean.opBoolean","INTERSECT",EDGE,{"disambiguationData":[OD(0.0)],"derivedFrom":[makeQuery(id+"F5.opExtrude","SWEPT_FACE",FACE,{"disambiguationData":[OSD([sQuery(id+"F4.wireOp",EDGE,"E30")])]}),makeQuery(id+"F8.opExtrude","SWEPT_FACE",FACE,{"disambiguationData":[OSD([sQuery(id+"F7.wireOp",EDGE,"E67")])]})]});
            fillet(context, id + "F14", {"entities" : qUnion([Q0, Q1, Q2, Q3, Q4, Q5]), "radius" : 3 * mm, "tangentPropagation" : true, "allowEdgeOverflow" : false});
        }
        {
            var Q0;
            Q0=makeQuery(id+"F1.opExtrude","CAP_EDGE",EDGE,{"disambiguationData":[OSD([sQuery(id+"F0.wireOp",EDGE,"E1.bottom")])],"isStart":false});
            fillet(context, id + "F15", {"entities" : qUnion([Q0]), "radius" : 2 * mm, "tangentPropagation" : true, "allowEdgeOverflow" : false});
        }
        {
            var Q0;
            {var subQ0=sQuery(id+"F0.wireOp",EDGE,"E21.filletArc");var subQ1=sQuery(id+"F0.wireOp",EDGE,"E7");var subQ2=sQuery(id+"F0.wireOp",EDGE,"E6");var subQ3=sQuery(id+"F0.wireOp",EDGE,"E5");var subQ4=sQuery(id+"F0.wireOp",EDGE,"E4");var subQ5=sQuery(id+"F0.wireOp",EDGE,"E22.filletArc");var subQ6=sQuery(id+"F0.wireOp",EDGE,"E1.bottom");var subQ7=sQuery(id+"F0.wireOp",EDGE,"E1.right");var subQ8=sQuery(id+"F0.wireOp",EDGE,"E1.top");var subQ9=sQuery(id+"F0.wireOp",EDGE,"E1.left");var subQ10=sQuery(id+"F0.wireOp",EDGE,"E23.filletArc");var subQ11=sQuery(id+"F0.wireOp",EDGE,"E24.filletArc");Q0=makeQuery(id+"F2.boolean.opBoolean","SPLIT",FACE,{"disambiguationData":[TD([makeQuery(id+"F1.opExtrude","SWEPT_FACE",FACE,{"disambiguationData":[OSD([subQ6])]})])],"derivedFrom":makeQuery(id+"F1.opExtrude","CAP_FACE",FACE,{"disambiguationData":[OSD([subQ6,subQ8,subQ9,subQ7,subQ4,subQ3,subQ2,subQ1,subQ0,subQ5,subQ10,subQ11])],"isStart":true})});}
            var sketch = newSketch(context, id + "F16", { "sketchPlane" : qUnion([Q0])});
            skLineSegment(sketch, "E79.0", {"start": v(-80, -80) * mm, "end": v(-80, 80) * mm});
            skLineSegment(sketch, "E79.1", {"start": v(-70, -90) * mm, "end": v(70, -90) * mm});
            skLineSegment(sketch, "E79.2", {"start": v(80, -80) * mm, "end": v(80, 80) * mm});
            skLineSegment(sketch, "E79.3", {"start": v(-70, 90) * mm, "end": v(70, 90) * mm});
            skArc(sketch, "E79.4", {"start": v(80, 80) * mm, "mid": v(77.07, 87.07) * mm, "end": v(70, 90) * mm});
            skArc(sketch, "E79.5", {"start": v(-70, 90) * mm, "mid": v(-77.07, 87.07) * mm, "end": v(-80, 80) * mm});
            skArc(sketch, "E79.6", {"start": v(-80, -80) * mm, "mid": v(-77.07, -87.07) * mm, "end": v(-70, -90) * mm});
            skArc(sketch, "E79.7", {"start": v(70, -90) * mm, "mid": v(77.07, -87.07) * mm, "end": v(80, -80) * mm});
            skCircle(sketch, "E79.8", {"center": v(60, -67.5) * mm, "radius": 4 * mm});
            skCircle(sketch, "E79.9", {"center": v(-60, -67.5) * mm, "radius": 4 * mm});
            skArc(sketch, "E79.10", {"start": v(-56.15, -48.18) * mm, "mid": v(0, -67.5) * mm, "end": v(56.15, -48.18) * mm});
            skLineSegment(sketch, "E79.11", {"start": v(-60, 40.3) * mm, "end": v(-60, -40.3) * mm});
            skArc(sketch, "E79.12", {"start": v(56.15, 48.18) * mm, "mid": v(0, 67.5) * mm, "end": v(-56.15, 48.18) * mm});
            skLineSegment(sketch, "E79.13", {"start": v(60, 40.3) * mm, "end": v(60, -40.3) * mm});
            skArc(sketch, "E79.14", {"start": v(56.15, -48.18) * mm, "mid": v(58.99, -44.68) * mm, "end": v(60, -40.3) * mm});
            skArc(sketch, "E79.15", {"start": v(-60, -40.3) * mm, "mid": v(-58.99, -44.68) * mm, "end": v(-56.15, -48.18) * mm});
            skArc(sketch, "E79.16", {"start": v(60, 40.3) * mm, "mid": v(58.99, 44.68) * mm, "end": v(56.15, 48.18) * mm});
            skArc(sketch, "E79.17", {"start": v(-56.15, 48.18) * mm, "mid": v(-58.99, 44.68) * mm, "end": v(-60, 40.3) * mm});
            skCircle(sketch, "E79.18", {"center": v(60, 67.5) * mm, "radius": 4 * mm});
            skCircle(sketch, "E79.19", {"center": v(-60, 67.5) * mm, "radius": 4 * mm});
            skLineSegment(sketch, "E80", {"start": v(0, 90) * mm, "end": v(0, 120) * mm, "construction": true});
            skPoint(sketch, "E80.endSnap0", {"position": v(0, 90) * mm});
            skCircle(sketch, "E81", {"center": v(0, 120) * mm, "radius": 6 * mm});
            skLineSegment(sketch, "E82", {"start": v(-33, 90) * mm, "end": v(-15, 108) * mm});
            skLineSegment(sketch, "E83", {"start": v(-15, 108) * mm, "end": v(-15, 120) * mm});
            skArc(sketch, "E84", {"start": v(-15, 120) * mm, "mid": v(0, 135) * mm, "end": v(15, 120) * mm});
            skLineSegment(sketch, "E85", {"start": v(15, 120) * mm, "end": v(15, 108) * mm});
            skLineSegment(sketch, "E86", {"start": v(15, 108) * mm, "end": v(33, 90) * mm});
            skLineSegment(sketch, "E87", {"start": v(-80, 0) * mm, "end": v(80, 0) * mm, "construction": true});
            skLineSegment(sketch, "E88.MirrorCS", {"start": v(-15, -108) * mm, "end": v(-15, -120) * mm});
            skLineSegment(sketch, "E89.MirrorCS", {"start": v(-33, -90) * mm, "end": v(-15, -108) * mm});
            skLineSegment(sketch, "E90.MirrorCS", {"start": v(15, -108) * mm, "end": v(33, -90) * mm});
            skLineSegment(sketch, "E91.MirrorCS", {"start": v(15, -120) * mm, "end": v(15, -108) * mm});
            skArc(sketch, "E92.MirrorCS", {"start": v(-15, -120) * mm, "mid": v(0, -135) * mm, "end": v(15, -120) * mm});
            skCircle(sketch, "E93.MirrorC", {"center": v(0, -120) * mm, "radius": 6 * mm});
            skLineSegment(sketch, "E94.MirrorCS", {"start": v(0, -90) * mm, "end": v(0, -120) * mm, "construction": true});
            skSolve(sketch);
        }
        {
            var Q0;
            Q0=makeQuery(id+"F16.imprint","IMPRINT",FACE,{"disambiguationData":[TD([[makeQuery(id+"F16.imprint","IMPRINT",EDGE,{"derivedFrom":sQuery(id+"F16.wireOp",EDGE,"E81")}),-1.0]])]});
            var Q1;
            Q1=makeQuery(id+"F16.imprint","IMPRINT",FACE,{"disambiguationData":[TD([[makeQuery(id+"F16.imprint","IMPRINT",EDGE,{"derivedFrom":sQuery(id+"F16.wireOp",EDGE,"E79.0")}),-1.0]])]});
            var Q2;
            Q2=makeQuery(id+"F16.imprint","IMPRINT",FACE,{"disambiguationData":[TD([[makeQuery(id+"F16.imprint","IMPRINT",EDGE,{"derivedFrom":sQuery(id+"F16.wireOp",EDGE,"E88.MirrorCS")}),1.0]])]});
            var Q3;
            Q3=makeQuery(id+"F2.opExtrude","CAP_FACE",FACE,{"disambiguationData":[OSD([sQuery(id+"F0.wireOp",EDGE,"E12"),sQuery(id+"F0.wireOp",EDGE,"E13"),sQuery(id+"F0.wireOp",EDGE,"E14"),sQuery(id+"F0.wireOp",EDGE,"E15"),sQuery(id+"F0.wireOp",EDGE,"E17.filletArc"),sQuery(id+"F0.wireOp",EDGE,"E18.filletArc"),sQuery(id+"F0.wireOp",EDGE,"E19.filletArc"),sQuery(id+"F0.wireOp",EDGE,"E20.filletArc"),sQuery(id+"F0.wireOp",EDGE,"E25.0"),sQuery(id+"F0.wireOp",EDGE,"E25.1"),sQuery(id+"F0.wireOp",EDGE,"E25.2"),sQuery(id+"F0.wireOp",EDGE,"E25.3"),sQuery(id+"F0.wireOp",EDGE,"E25.4"),sQuery(id+"F0.wireOp",EDGE,"E25.5"),sQuery(id+"F0.wireOp",EDGE,"E25.6"),sQuery(id+"F0.wireOp",EDGE,"E25.7")])],"isStart":false});
            extrude(context, id + "F17", {"entities" : qUnion([Q0, Q1, Q2]), "endBound" : BoundingType.UP_TO_SURFACE, "endBoundEntityFace" : qUnion([Q3]), "depth" : 25 * mm});
        }
    });
